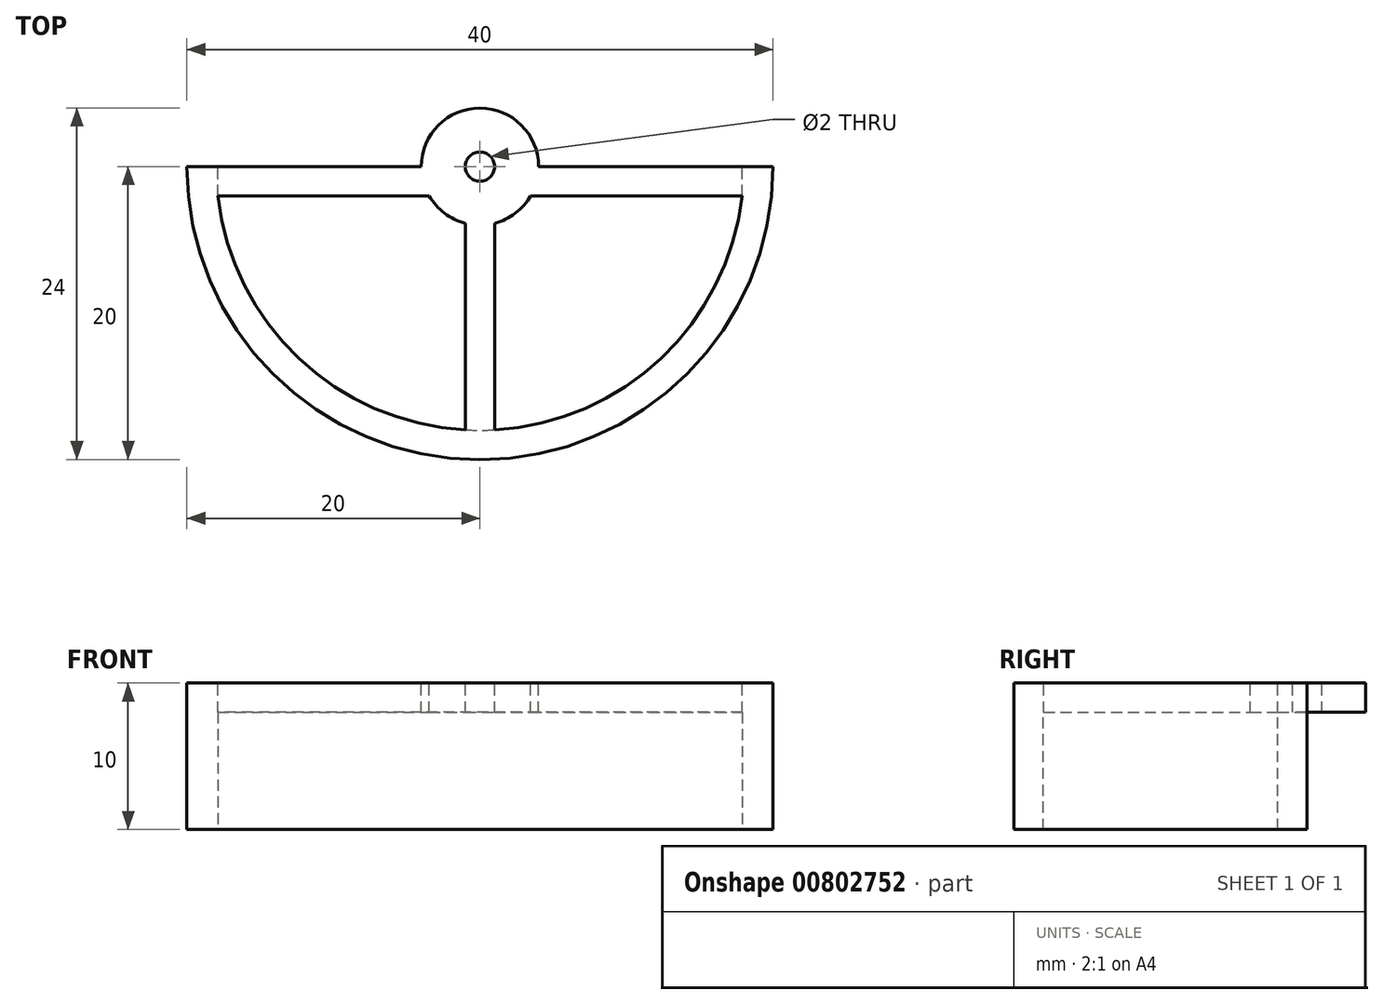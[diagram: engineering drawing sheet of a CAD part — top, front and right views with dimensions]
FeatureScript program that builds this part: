
annotation { "Feature Type Name" : "Feature", "Feature Type Description" : "" }
export const myFeature = defineFeature(function(context is Context, id is Id, definition is map)
    precondition{}
    {
        {
            var Q0;
            Q0=qCreatedBy(makeId("Top.planeOp"),FACE);
            var sketch = newSketch(context, id + "F0", { "sketchPlane" : qUnion([Q0])});
            skCircle(sketch, "E0", {"center": v(0, 0) * mm, "radius": 20 * mm});
            skSolve(sketch);
        }
        {
            var Q0;
            Q0 = qSketchRegion(id + "F0", true);
            extrude(context, id + "F1", {"entities" : qUnion([Q0]), "depth" : 10 * mm, "offsetDistance" : 25 * mm});
        }
        {
            var Q0;
            Q0=makeQuery(id+"F1.opExtrude","CAP_FACE",FACE,{"disambiguationData":[OSD([sQuery(id+"F0.wireOp",EDGE,"E0")])],"isStart":false});
            var sketch = newSketch(context, id + "F2", { "sketchPlane" : qUnion([Q0])});
            skLineSegment(sketch, "E1", {"start": v(0, 0) * mm, "end": v(20, 0) * mm});
            skLineSegment(sketch, "E2", {"start": v(0, 0) * mm, "end": v(-20, 0) * mm});
            skArc(sketch, "E3", {"start": v(-20, 0) * mm, "mid": v(0, 20) * mm, "end": v(20, 0) * mm});
            skSolve(sketch);
        }
        {
            var Q0;
            Q0 = qSketchRegion(id + "F2", true);
            extrude(context, id + "F3", {"entities" : qUnion([Q0]), "operationType" : NewBodyOperationType.REMOVE, "oppositeDirection" : true, "depth" : 25 * mm, "offsetDistance" : 25 * mm});
        }
        {
            var Q0;
            Q0 = qSketchRegion(id + "F2", true);
            extrude(context, id + "F4", {"entities" : qUnion([Q0]), "operationType" : NewBodyOperationType.REMOVE, "oppositeDirection" : true, "depth" : 25 * mm, "offsetDistance" : 25 * mm});
        }
        {
            var Q0;
            Q0=makeQuery(id+"F1.opExtrude","CAP_FACE",FACE,{"disambiguationData":[OSD([sQuery(id+"F0.wireOp",EDGE,"E0")])],"isStart":false});
            var sketch = newSketch(context, id + "F5", { "sketchPlane" : qUnion([Q0])});
            skArc(sketch, "E4", {"start": v(17.89, -2) * mm, "mid": v(0, -18) * mm, "end": v(-17.89, -2) * mm});
            skLineSegment(sketch, "E5.top", {"start": v(-17.89, -2) * mm, "end": v(17.89, -2) * mm});
            skPoint(sketch, "E6.orphan", {"position": v(18, 0) * mm});
            skSolve(sketch);
        }
        {
            var Q0;
            Q0 = qSketchRegion(id + "F5", true);
            extrude(context, id + "F6", {"entities" : qUnion([Q0]), "operationType" : NewBodyOperationType.REMOVE, "oppositeDirection" : true, "depth" : 25 * mm, "offsetDistance" : 25 * mm});
        }
        {
            var Q0;
            Q0=makeQuery(id+"F1.opExtrude","CAP_FACE",FACE,{"disambiguationData":[OSD([sQuery(id+"F0.wireOp",EDGE,"E0")])],"isStart":true});
            var sketch = newSketch(context, id + "F7", { "sketchPlane" : qUnion([Q0])});
            skLineSegment(sketch, "E7.bottom", {"start": v(17.89, 2) * mm, "end": v(-17.89, 2) * mm});
            skLineSegment(sketch, "E7.top", {"start": v(17.89, 0) * mm, "end": v(-17.89, 0) * mm});
            skLineSegment(sketch, "E7.left", {"start": v(17.89, 2) * mm, "end": v(17.89, 0) * mm});
            skLineSegment(sketch, "E7.right", {"start": v(-17.89, 2) * mm, "end": v(-17.89, 0) * mm});
            skSolve(sketch);
        }
        {
            var Q0;
            Q0 = qSketchRegion(id + "F7", true);
            extrude(context, id + "F8", {"entities" : qUnion([Q0]), "operationType" : NewBodyOperationType.REMOVE, "oppositeDirection" : true, "depth" : 8 * mm, "offsetDistance" : 25 * mm});
        }
        {
            var Q0;
            Q0=makeQuery(id+"F1.opExtrude","CAP_FACE",FACE,{"disambiguationData":[OSD([sQuery(id+"F0.wireOp",EDGE,"E0")])],"isStart":false});
            var sketch = newSketch(context, id + "F9", { "sketchPlane" : qUnion([Q0])});
            skLineSegment(sketch, "E8.bottom", {"start": v(1, -19.97) * mm, "end": v(-1, -19.97) * mm});
            skLineSegment(sketch, "E8.left", {"start": v(1, -19.97) * mm, "end": v(1, -2) * mm});
            skLineSegment(sketch, "E8.right", {"start": v(-1, -19.97) * mm, "end": v(-1, -2) * mm});
            skPoint(sketch, "E8.middle", {"position": v(0, -2) * mm});
            skLineSegment(sketch, "E9", {"start": v(-1, -2) * mm, "end": v(1, -2) * mm});
            skPoint(sketch, "E8.top.start.orphan", {"position": v(1, 15.97) * mm});
            skPoint(sketch, "E10.orphan", {"position": v(-1, 15.97) * mm});
            skSolve(sketch);
        }
        {
            var Q0;
            Q0 = qSketchRegion(id + "F9", true);
            extrude(context, id + "F10", {"entities" : qUnion([Q0]), "operationType" : NewBodyOperationType.ADD, "oppositeDirection" : true, "depth" : 2 * mm, "offsetDistance" : 25 * mm});
        }
        {
            var Q0;
            Q0=makeQuery(id+"F10.boolean.opBoolean","MERGE",FACE,{"derivedFrom":[makeQuery(id+"F1.opExtrude","CAP_FACE",FACE,{"disambiguationData":[OSD([sQuery(id+"F0.wireOp",EDGE,"E0")])],"isStart":false}),makeQuery(id+"F10.opExtrude","CAP_FACE",FACE,{"disambiguationData":[OSD([sQuery(id+"F9.wireOp",EDGE,"E8.bottom"),sQuery(id+"F9.wireOp",EDGE,"E8.left"),sQuery(id+"F9.wireOp",EDGE,"E8.right"),sQuery(id+"F9.wireOp",EDGE,"E9")])],"isStart":true})]});
            var sketch = newSketch(context, id + "F11", { "sketchPlane" : qUnion([Q0])});
            skCircle(sketch, "E11", {"center": v(0, 0) * mm, "radius": 4 * mm});
            skSolve(sketch);
        }
        {
            var Q0;
            Q0 = qSketchRegion(id + "F11", true);
            extrude(context, id + "F12", {"entities" : qUnion([Q0]), "operationType" : NewBodyOperationType.ADD, "oppositeDirection" : true, "depth" : 2 * mm, "offsetDistance" : 25 * mm});
        }
        {
            var Q0;
            Q0=makeQuery(id+"F12.boolean.opBoolean","MERGE",FACE,{"derivedFrom":[makeQuery(id+"F10.boolean.opBoolean","MERGE",FACE,{"derivedFrom":[makeQuery(id+"F1.opExtrude","CAP_FACE",FACE,{"disambiguationData":[OSD([sQuery(id+"F0.wireOp",EDGE,"E0")])],"isStart":false}),makeQuery(id+"F10.opExtrude","CAP_FACE",FACE,{"disambiguationData":[OSD([sQuery(id+"F9.wireOp",EDGE,"E8.bottom"),sQuery(id+"F9.wireOp",EDGE,"E8.left"),sQuery(id+"F9.wireOp",EDGE,"E8.right"),sQuery(id+"F9.wireOp",EDGE,"E9")])],"isStart":true})]}),makeQuery(id+"F12.opExtrude","CAP_FACE",FACE,{"disambiguationData":[OSD([sQuery(id+"F11.wireOp",EDGE,"E11")])],"isStart":true})]});
            var sketch = newSketch(context, id + "F13", { "sketchPlane" : qUnion([Q0])});
            skCircle(sketch, "E12", {"center": v(0, 0) * mm, "radius": 1 * mm});
            skSolve(sketch);
        }
        {
            var Q0;
            Q0 = qSketchRegion(id + "F13", true);
            extrude(context, id + "F14", {"entities" : qUnion([Q0]), "operationType" : NewBodyOperationType.REMOVE, "oppositeDirection" : true, "depth" : 25 * mm, "offsetDistance" : 25 * mm});
        }
    });
